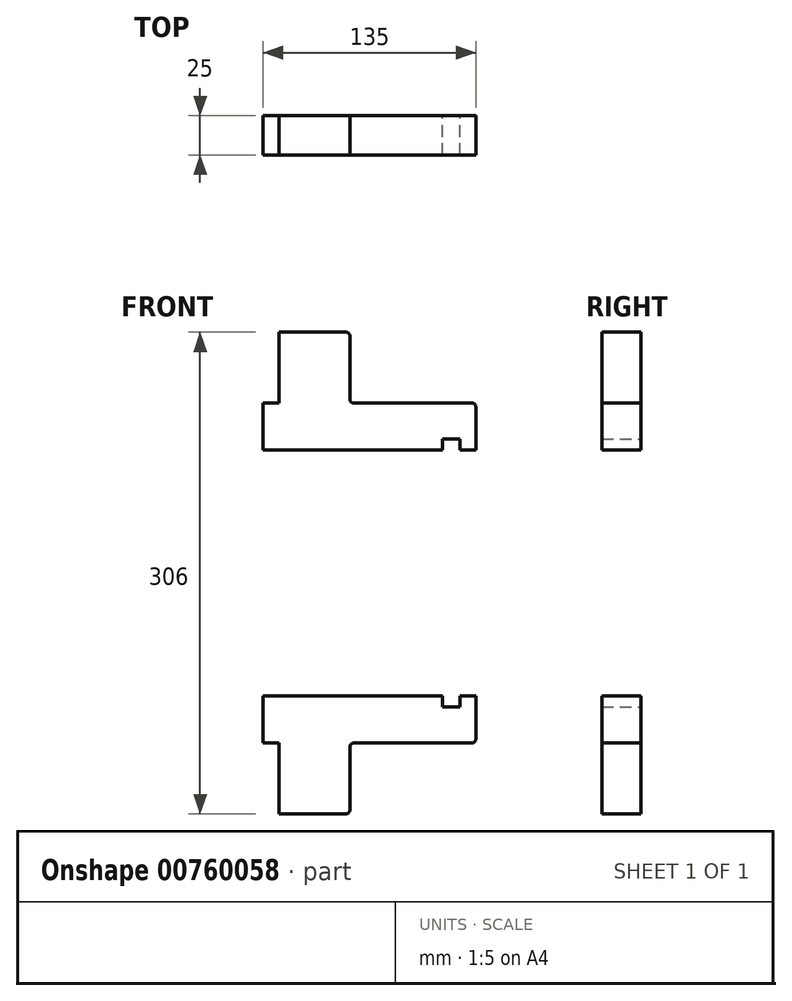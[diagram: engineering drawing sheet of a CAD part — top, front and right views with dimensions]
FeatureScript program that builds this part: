
annotation { "Feature Type Name" : "Feature", "Feature Type Description" : "" }
export const myFeature = defineFeature(function(context is Context, id is Id, definition is map)
    precondition{}
    {
        {
            var Q0;
            Q0=qCreatedBy(makeId("Front.planeOp"),FACE);
            var sketch = newSketch(context, id + "F0", { "sketchPlane" : qUnion([Q0])});
            skLineSegment(sketch, "E0", {"start": v(0, 0) * mm, "end": v(0, -7.08) * mm});
            skLineSegment(sketch, "E1", {"start": v(0, -7.08) * mm, "end": v(11.07, -7.08) * mm});
            skLineSegment(sketch, "E2", {"start": v(11.07, -7.08) * mm, "end": v(11.07, 0) * mm});
            skLineSegment(sketch, "E3", {"start": v(11.07, 0) * mm, "end": v(21.07, 0) * mm});
            skLineSegment(sketch, "E4", {"start": v(21.07, 0) * mm, "end": v(21.07, -30) * mm});
            skLineSegment(sketch, "E5", {"start": v(21.07, -30) * mm, "end": v(-58.93, -30) * mm});
            skLineSegment(sketch, "E6", {"start": v(-58.93, -30) * mm, "end": v(-58.93, -75) * mm});
            skLineSegment(sketch, "E7", {"start": v(-58.93, -75) * mm, "end": v(-103.93, -75) * mm});
            skLineSegment(sketch, "E8", {"start": v(-103.93, -75) * mm, "end": v(-103.93, -30) * mm});
            skLineSegment(sketch, "E9", {"start": v(-103.93, -30) * mm, "end": v(-113.93, -30) * mm});
            skLineSegment(sketch, "E10", {"start": v(-113.93, -30) * mm, "end": v(-113.93, 0) * mm});
            skLineSegment(sketch, "E11", {"start": v(-113.93, 0) * mm, "end": v(0, 0) * mm});
            skLineSegment(sketch, "E12", {"start": v(-129.42, 78) * mm, "end": v(36.85, 78) * mm, "construction": true});
            skLineSegment(sketch, "E13.MirrorCS", {"start": v(11.07, 163.08) * mm, "end": v(11.07, 156) * mm});
            skLineSegment(sketch, "E14.MirrorCS", {"start": v(11.07, 156) * mm, "end": v(21.07, 156) * mm});
            skLineSegment(sketch, "E15.MirrorCS", {"start": v(0, 156) * mm, "end": v(0, 163.08) * mm});
            skLineSegment(sketch, "E16.MirrorCS", {"start": v(0, 163.08) * mm, "end": v(11.07, 163.08) * mm});
            skLineSegment(sketch, "E17.MirrorCS", {"start": v(21.07, 156) * mm, "end": v(21.07, 186) * mm});
            skLineSegment(sketch, "E18.MirrorCS", {"start": v(-113.93, 156) * mm, "end": v(0, 156) * mm});
            skLineSegment(sketch, "E19.MirrorCS", {"start": v(-113.93, 186) * mm, "end": v(-113.93, 156) * mm});
            skLineSegment(sketch, "E20.MirrorCS", {"start": v(-103.93, 186) * mm, "end": v(-113.93, 186) * mm});
            skLineSegment(sketch, "E21.MirrorCS", {"start": v(-58.93, 231) * mm, "end": v(-103.93, 231) * mm});
            skLineSegment(sketch, "E22.MirrorCS", {"start": v(21.07, 186) * mm, "end": v(-58.93, 186) * mm});
            skLineSegment(sketch, "E23.MirrorCS", {"start": v(-103.93, 231) * mm, "end": v(-103.93, 186) * mm});
            skLineSegment(sketch, "E24.MirrorCS", {"start": v(-58.93, 186) * mm, "end": v(-58.93, 231) * mm});
            skSolve(sketch);
        }
        {
            var Q0;
            Q0=makeQuery(id+"F0.imprint","IMPRINT",FACE,{"disambiguationData":[TD([[makeQuery(id+"F0.imprint","IMPRINT",EDGE,{"derivedFrom":sQuery(id+"F0.wireOp",EDGE,"E13.MirrorCS")}),1.0]])]});
            var Q1;
            Q1=makeQuery(id+"F0.imprint","IMPRINT",FACE,{"disambiguationData":[TD([[makeQuery(id+"F0.imprint","IMPRINT",EDGE,{"derivedFrom":sQuery(id+"F0.wireOp",EDGE,"E0")}),-1.0]])]});
            extrude(context, id + "F1", {"entities" : qUnion([Q0, Q1]), "depth" : 25 * mm, "offsetDistance" : 25 * mm});
        }
        {
            var Q0;
            Q0=makeQuery(id+"F1.opExtrude","SWEPT_EDGE",EDGE,{"disambiguationData":[OSD([sQuery(id+"F0.wireOp",EDGE,"E21.MirrorCS"),sQuery(id+"F0.wireOp",EDGE,"E24.MirrorCS")])]});
            var Q1;
            Q1=makeQuery(id+"F1.opExtrude","SWEPT_EDGE",EDGE,{"disambiguationData":[OSD([sQuery(id+"F0.wireOp",EDGE,"E22.MirrorCS"),sQuery(id+"F0.wireOp",EDGE,"E24.MirrorCS")])]});
            var Q2;
            Q2=makeQuery(id+"F1.opExtrude","SWEPT_EDGE",EDGE,{"disambiguationData":[OSD([sQuery(id+"F0.wireOp",EDGE,"E17.MirrorCS"),sQuery(id+"F0.wireOp",EDGE,"E22.MirrorCS")])]});
            var Q3;
            Q3=makeQuery(id+"F1.opExtrude","SWEPT_EDGE",EDGE,{"disambiguationData":[OSD([sQuery(id+"F0.wireOp",EDGE,"E4"),sQuery(id+"F0.wireOp",EDGE,"E5")])]});
            var Q4;
            Q4=makeQuery(id+"F1.opExtrude","SWEPT_EDGE",EDGE,{"disambiguationData":[OSD([sQuery(id+"F0.wireOp",EDGE,"E5"),sQuery(id+"F0.wireOp",EDGE,"E6")])]});
            var Q5;
            Q5=makeQuery(id+"F1.opExtrude","SWEPT_EDGE",EDGE,{"disambiguationData":[OSD([sQuery(id+"F0.wireOp",EDGE,"E6"),sQuery(id+"F0.wireOp",EDGE,"E7")])]});
            fillet(context, id + "F2", {"entities" : qUnion([Q0, Q1, Q2, Q3, Q4, Q5]), "radius" : 2.5 * mm, "tangentPropagation" : true, "allowEdgeOverflow" : false});
        }
    });
